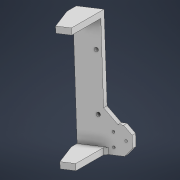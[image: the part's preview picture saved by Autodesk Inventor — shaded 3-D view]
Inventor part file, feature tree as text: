
AUTODESK INVENTOR PART (.ipt)
format: ipt  version: 2021 (Build 250183000, 183)  size: 172,544 bytes
history: native  units: mm
features: extrude x4, chamfer x4, sketch x4, other x1, mirror x1
ambient origin geometry x8: Origin, YZ Plane, XZ Plane, XY Plane, X Axis, Y Axis, Z Axis, Center Point
bodies: Solid1 (feature_tree)
feature tree (14):
  other  "psu holder left.ipt"
  extrude  "Extrusion1"  Depth=25.0mm
  extrude  "Extrusion2"  Depth=25.0mm
  mirror  "Mirror1"
  extrude  "Extrusion3"  TaperAngle=0.0deg  [1 undecoded]
  chamfer  "Chamfer1"  Distance=59.5mm
  chamfer  "Chamfer2"  [1 undecoded]
  chamfer  "Chamfer3"  Distance=25.0mm
  chamfer  "Chamfer4"  Distance=26.0mm
  extrude  "Extrusion4"  Depth=2.0mm
  sketch  "Sketch1"  dims[d0=10.0mm d1=25.0mm]
  sketch  "Sketch2"  dims[d2=25.0mm d3=25.0mm]
  sketch  "Sketch3"  dims[d4=6.0mm d5=0.0mm]
  sketch  "Sketch4"  dims[d10=6.0mm d11=59.5mm d12=0.0mm d13=25.0mm d14=26.0mm d15=13.0mm d16=12.0mm d17=15.0mm d18=2.5mm d19=30.0mm d21=360.0deg d23=6.0mm d24=0.0mm d25=7.5mm d26=2.0mm d27=45.0deg d28=12.5mm d29=2.0mm d30=45.0deg d31=3.0mm d32=2.0mm d33=45.0deg d34=40.0mm d35=40.0mm d36=15.0deg d37=5.0mm d38=4.0mm d39=4.0mm d40=54.0mm d41=26.5mm d42=26.5mm d43=0.0mm d44=0.0mm d9=0.5mm]
note: 2 required parameter values undecoded (feature->parameter linkage not recoverable at this tier; creation-order binding heuristic only, values carry confidence <= 0.55)
